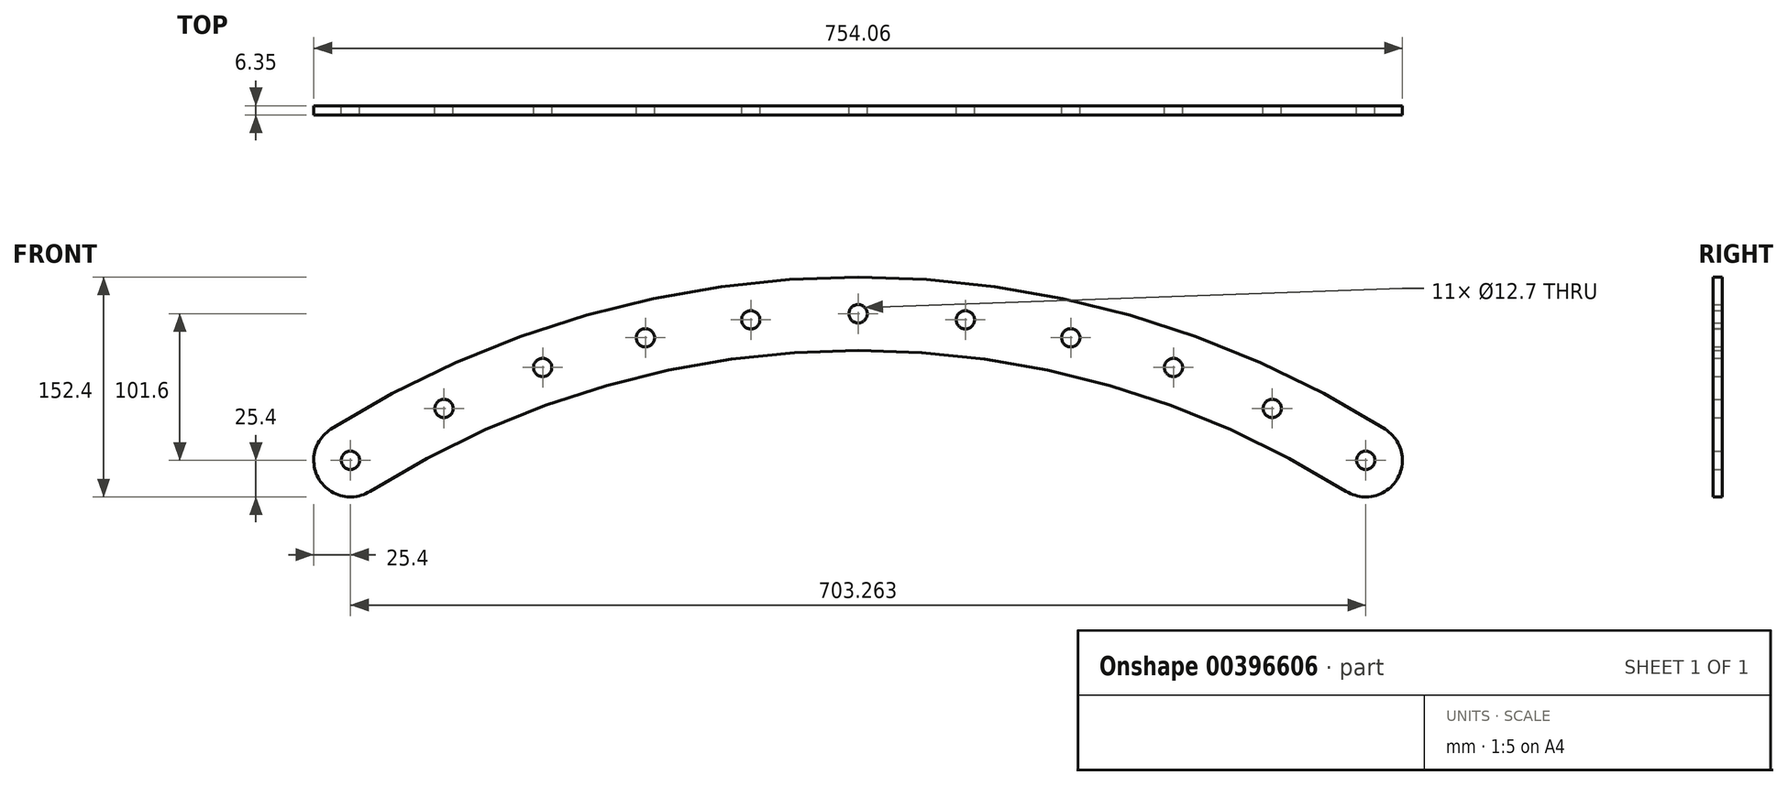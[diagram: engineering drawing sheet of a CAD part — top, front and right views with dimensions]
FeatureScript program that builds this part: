
annotation { "Feature Type Name" : "Feature", "Feature Type Description" : "" }
export const myFeature = defineFeature(function(context is Context, id is Id, definition is map)
    precondition{}
    {
        {
            var Q0;
            Q0=qCreatedBy(makeId("Front.planeOp"),FACE);
            var sketch = newSketch(context, id + "F0", { "sketchPlane" : qUnion([Q0])});
            skCircle(sketch, "E0", {"center": v(0, 0) * mm, "radius": 6.35 * mm});
            skCircle(sketch, "E1", {"center": v(703.26, 0) * mm, "radius": 6.35 * mm});
            skCircle(sketch, "E2", {"center": v(351.63, 101.6) * mm, "radius": 6.35 * mm});
            skArc(sketch, "E3.0", {"start": v(716.8, 21.49) * mm, "mid": v(351.63, 127) * mm, "end": v(-13.55, 21.49) * mm});
            skArc(sketch, "E4.0", {"start": v(689.72, -21.49) * mm, "mid": v(351.63, 76.2) * mm, "end": v(13.55, -21.49) * mm});
            skCircle(sketch, "E5", {"center": v(64.77, 35.92) * mm, "radius": 6.35 * mm});
            skCircle(sketch, "E6", {"center": v(133.16, 64.35) * mm, "radius": 6.35 * mm});
            skCircle(sketch, "E7", {"center": v(204.3, 84.93) * mm, "radius": 6.35 * mm});
            skCircle(sketch, "E8", {"center": v(277.32, 97.4) * mm, "radius": 6.35 * mm});
            skCircle(sketch, "E9", {"center": v(425.95, 97.4) * mm, "radius": 6.35 * mm});
            skCircle(sketch, "E10", {"center": v(498.95, 84.93) * mm, "radius": 6.35 * mm});
            skCircle(sketch, "E11", {"center": v(570.1, 64.35) * mm, "radius": 6.35 * mm});
            skCircle(sketch, "E12", {"center": v(638.5, 35.92) * mm, "radius": 6.35 * mm});
            skArc(sketch, "E13", {"start": v(716.8, 21.49) * mm, "mid": v(724.75, -13.55) * mm, "end": v(689.72, -21.49) * mm});
            skArc(sketch, "E14", {"start": v(-13.55, 21.49) * mm, "mid": v(-21.49, -13.55) * mm, "end": v(13.55, -21.49) * mm});
            skSolve(sketch);
        }
        {
            var Q0;
            Q0=makeQuery(id+"F0.imprint","IMPRINT",FACE,{"disambiguationData":[TD([[makeQuery(id+"F0.imprint","IMPRINT",EDGE,{"derivedFrom":sQuery(id+"F0.wireOp",EDGE,"E0")}),-1.0]])]});
            extrude(context, id + "F1", {"entities" : qUnion([Q0]), "depth" : 6.35 * mm});
        }
    });
